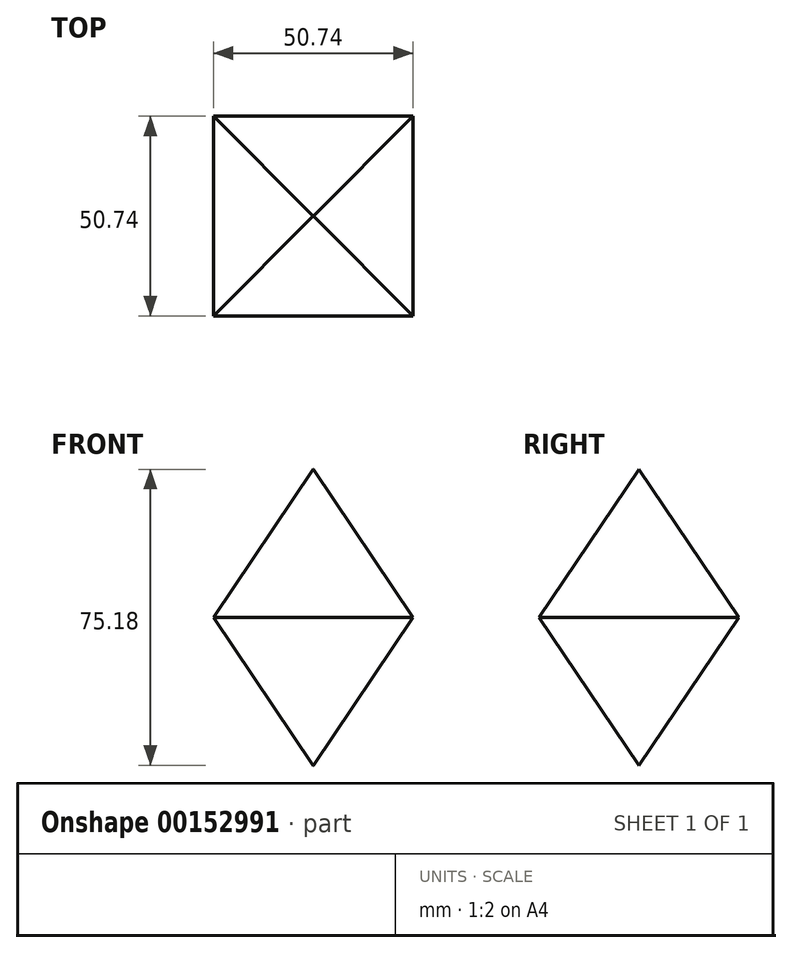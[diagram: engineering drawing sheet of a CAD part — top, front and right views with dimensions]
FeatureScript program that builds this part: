
annotation { "Feature Type Name" : "Feature", "Feature Type Description" : "" }
export const myFeature = defineFeature(function(context is Context, id is Id, definition is map)
    precondition{}
    {
        {
            var Q0;
            Q0=qCreatedBy(makeId("Top.planeOp"),FACE);
            var sketch = newSketch(context, id + "F0", { "sketchPlane" : qUnion([Q0])});
            skLineSegment(sketch, "E0.bottom", {"start": v(-34.3, 34.3) * mm, "end": v(34.3, 34.3) * mm});
            skLineSegment(sketch, "E0.top", {"start": v(-34.3, -34.3) * mm, "end": v(34.3, -34.3) * mm});
            skLineSegment(sketch, "E0.left", {"start": v(-34.3, 34.3) * mm, "end": v(-34.3, -34.3) * mm});
            skLineSegment(sketch, "E0.right", {"start": v(34.3, 34.3) * mm, "end": v(34.3, -34.3) * mm});
            skPoint(sketch, "E0.middle", {"position": v(0, 0) * mm});
            skSolve(sketch);
        }
        {
            var Q0;
            Q0 = qSketchRegion(id + "F0", true);
            extrude(context, id + "F1", {"entities" : qUnion([Q0]), "depth" : 50.8 * mm, "hasDraft" : true, "draftAngle" : 34 * degree, "draftPullDirection" : true});
        }
        {
            var Q0;
            Q0=makeQuery(id+"F1.opExtrude","SWEPT_BODY",BODY,{"disambiguationData":[OSD([sQuery(id+"F0.wireOp",EDGE,"E0.bottom"),sQuery(id+"F0.wireOp",EDGE,"E0.top"),sQuery(id+"F0.wireOp",EDGE,"E0.left"),sQuery(id+"F0.wireOp",EDGE,"E0.right")])]});
            var Q1;
            Q1=qCreatedBy(makeId("Origin.pointOp"),VERTEX);
            transform(context, id + "F2", {"entities" : qUnion([Q0]), "transformType" : TransformType.SCALE_UNIFORMLY, "scale" : .74, "scalePoint" : qUnion([Q1]), "makeCopy" : false});
        }
        {
            var Q0;
            Q0=makeQuery(id+"F1.opExtrude","SWEPT_BODY",BODY,{"disambiguationData":[OSD([sQuery(id+"F0.wireOp",EDGE,"E0.bottom"),sQuery(id+"F0.wireOp",EDGE,"E0.top"),sQuery(id+"F0.wireOp",EDGE,"E0.left"),sQuery(id+"F0.wireOp",EDGE,"E0.right")])]});
            var Q1;
            Q1=qCreatedBy(makeId("Top.planeOp"),FACE);
            mirror(context, id + "F3", {"operationType" : NewBodyOperationType.ADD, "entities" : qUnion([Q0]), "mirrorPlane" : qUnion([Q1])});
        }
    });
